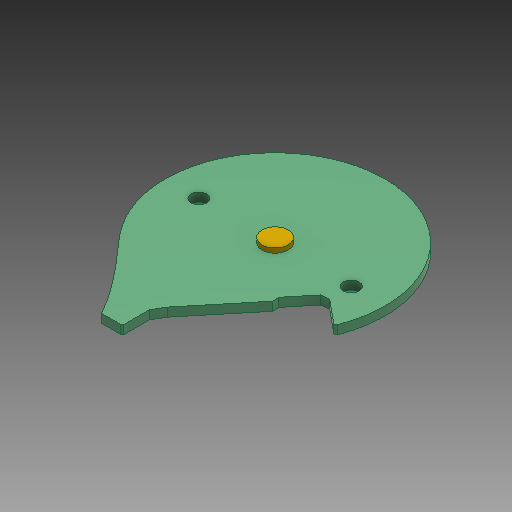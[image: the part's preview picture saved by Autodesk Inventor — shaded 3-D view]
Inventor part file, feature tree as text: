
AUTODESK INVENTOR PART (.ipt)
format: ipt  version: 2019 (Build 230136000, 136)  size: 2,604,032 bytes
history: native  units: mm
features: extrude x3, sketch x2, fillet x1, other x1
ambient origin geometry x8: Origin, YZ Plane, XZ Plane, XY Plane, X Axis, Y Axis, Z Axis, Center Point
bodies: Volumenkörper1 (feature_tree)
feature tree (7):
  extrude  "Extrusion1"  Depth=1.0mm TaperAngle=0.0deg
  fillet  "Rundung1"  Radius=0.2mm
  extrude  "Extrusion2"  Depth=0.5mm TaperAngle=0.0deg
  extrude  "Extrusion3"  Depth=10.0mm
  sketch  "Skizze1"  dims[d0=25.25mm d43=1.0mm d44=0.0mm d45=0.2mm]
  other  "Bild1"
  sketch  "Skizze3"  dims[d46=3.0mm d47=0.5mm d48=0.0mm d49=17.5mm d50=8.75mm d51=1.8mm d52=1.8mm d53=10.0mm d54=0.0mm]
